# Revit family: 75023
name_source: partatom
category: Doors
revit_build: Autodesk Revit 2018 (Build: 20170223_1515(x64)
units: mm (PartAtom-declared; Revit-internal decimal feet)

## family parameters
Always vertical = Yes
Cut with Voids When Loaded = No
Host = Wall
OmniClass Number = 23.30.10.17.17
OmniClass Title = Folding Doors and Grilles
Room Calculation Point = No
Shared = No

## types (1)
- Standard
    04 CSI = 08 41 13
    95 CSI = 8411
    Angle = 60.00°
    Assembly Code = B2050.1040
    Cost Info = http://www.nanawall.com
    Description = BeyondLiftSlide, SwingSlide Single Track Wood Framed Sliding System
    Engineering Details URL = http://www.nanawall.com
    Exterior Wall Offset = 0"
    Filler = Rubber - NanaWall - Black
    Function = Interior
    Glass Material = Glass - NanaWall - Generic
    Height = 144"
    Height Constraint = 118"
    Installation and Service URL = http://www.nanawall.com
    Manufacturer = NanaWall Systems, Inc.
    Manufacturer Fax = (415) 383-0312
    Max Panel Height = 113 65/128"
    Model = BeyondLiftSlide
    NanaWall Configurator = http://www.nanawall.com
    Opening Width = 139 51/128"
    Panel Height = 113 65/128"
    Performance URL = http://www.nanawall.com
    Product Page URL = http://www.nanawall.com
    Rough Height = 113 65/128"
    Rough Width = 142 7/64"
    Sash = Metal - NanaWall - Aluminum
    Subcategory = Folding Door
    Thickness = 2 5/8"
    URL = http://www.nanawall.com
    Wall Closure = By host
    Warranty URL = http://www.nanawall.com
    Width = 144"

## geometry (parser evidence)
native form markers: Blend x2, Sweep x25
no freeform markers — native parametric forms only
